# Revit family: CADS_Vent-Axia_DMEV C 100_125
name_source: partatom
category: Mechanical Equipment
revit_build: Autodesk Revit 2017 (Build: 20160720_1515(x64)
units: mm (PartAtom-declared; Revit-internal decimal feet)

## family parameters
Cut with Voids When Loaded = No
Host = Face
Part Type = Normal
Room Calculation Point = No
Round Connector Dimension = Use Diameter
Shared = No

## types (4) — shared parameters
AirflowRateRange = 0 CFM
Apparent Load = 6 VA
AssemblyPlace = UNKNOWN
AssetType = Fixed
Category = Pr_60_67_29_05:Axial flow fans
Default Elevation = 1800 mm  [stored 5.90551 ft]
DevelopedFor = Vent-Axia
DiffuserMaterial = Vent-Axia_Frosted
DurationUnit = year
Fansize = 90 mm
Fitting Type = Ignore
GrossWeight = 0.00 kg
HasProtectiveEarth = No
IfcExportAs = IfcFanType
IfcExportType = NOTDEFINED
IsExtendedWarranty = No
LightFixtureMaterial = Vent-Axia_White
Manufacturer = Vent-Axia Limited
Material = Die-cast aluminium
Name = dMEV Unit
NominalHeight = 190 mm
NominalLength = 190 mm
NominalWidth = 135 mm  [stored 0.442913 ft]
NumberOfPoles = 1
ProductionYear = 2020
Quantity = 1
RatedCurrent = 0.05 A
RatedVoltage = 230 V
ReflectorMaterial = Vent-Axia_Chrome
Shape = Square
Status = New
Type Image = <None>
URL = http://www.vent-axia.com
Version = 1.0
WarrantyDurationLabor = 2
WarrantyDurationMotors = 5
WarrantyDurationParts = 2
WarrantyDurationUnit = year
WorkingPressure = 0.00 in-wg
zero-valued in all types: CADS_Index, ExpectedServiceLife

## per-type parameters (varying)
| type | Body Connector | Body Depth | Body Rad | Model | ModelNumber | Spigot Dia | Spigot Length | Spigot Rad |
| NBR DMEV C 100 | 37 mm  [stored 0.121391 ft] | 54 mm  [stored 0.177165 ft] | 97.5 mm  [stored 0.319882 ft] | 498095 | 498095 | 100 mm  [stored 0.328084 ft] | -56 mm  [stored -0.183727 ft] | 49.5 mm  [stored 0.162402 ft] |
| NBR DMEV C 100HT | 37 mm  [stored 0.121391 ft] | 54 mm  [stored 0.177165 ft] | 97.5 mm  [stored 0.319882 ft] | 498096 | 498096 | 100 mm  [stored 0.328084 ft] | -56 mm  [stored -0.183727 ft] | 49.5 mm  [stored 0.162402 ft] |
| NBR DMEV C 125 | 43 mm  [stored 0.141076 ft] | 57 mm  [stored 0.187008 ft] | 109 mm  [stored 0.357612 ft] | 498097 | 498097 | 125 mm  [stored 0.410105 ft] | -75 mm | 62 mm  [stored 0.203412 ft] |
| NBR DMEV C 125HT | 43 mm  [stored 0.141076 ft] | 57 mm  [stored 0.187008 ft] | 109 mm  [stored 0.357612 ft] | 498098 | 498098 | 125 mm  [stored 0.410105 ft] | -75 mm | 62 mm  [stored 0.203412 ft] |

note: column(s) folded — value = type name in every type: Description, ModelReference

note: [stored X ft] marks values corroborated as IEEE doubles in the binary element streams (Revit-internal decimal feet)

## geometry (parser evidence)
native form markers: Blend x2, Sweep x2
no freeform markers — native parametric forms only
